# Revit family: Toilet_Seat-Elongated_Closed_Front-KOHLER-E480-K-32330_1
name_source: partatom
category: Plumbing Fixtures
units: mm (PartAtom-declared; Revit-internal decimal feet)

## family parameters
Cut with Voids When Loaded = No
Host = Face
OmniClass Number = 23.31.19.19.17
OmniClass Title = Water Closet Seats
Part Type = Normal
Room Calculation Point = No
Round Connector Dimension = Use Diameter
Shared = No

## types (1)
- 0-White
    ADA Compliant = No
    Apparent Load = 1800 VA
    Assembly Code = D2010
    CW Connection = Yes
    Cold Water Inlet = Cold Water Inlet
    Date Modified = 11/08/2022
    Default Elevation = 15"
    Description = BN330 Bidet Seat
    Drain Included = No
    Electrical Connector = Yes
    Electrical Note = One Dedicated Circuit Required
    Finish = Kohler-Plastic-0-White
    Flow Rate = 0 GPM
    HW Connection = No
    Height = 5"
    Hot Water Inlet = Hot Water Inlet
    Length = 20 7/8"
    Manufacturer = Kohler Co.
    Master Format 2014 = 22 41 39
    Master Format 2014 Name = Residential Faucets, Supplies, and Trim
    Material = Plastic
    Model = K-32330-0
    Pressure = 0.00 psi
    Product Documentation Link = https://www.us.kohler.com
    Product Name = E480
    Product Page URL = http://www.us.kohler.com
http://www.us.kohler.com
    Type = 1
    URL = https://www.us.kohler.com
    Vent Connection = No
    Voltage = 120 V
    Waste Connection = No
    Waste Water Outlet = Waste Water Outlet
    WaterSense Certified = No
    Width = 15 3/16"

## geometry (parser evidence)
native form markers: Sweep x5
no freeform markers — native parametric forms only
